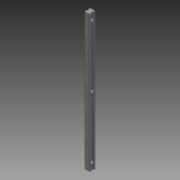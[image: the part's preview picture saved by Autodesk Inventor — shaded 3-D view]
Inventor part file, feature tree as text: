
AUTODESK INVENTOR PART (.ipt)
format: ipt  version: 2014 SP2 (Build 180246200, 246)  size: 133,120 bytes
history: native  units: mm
features: other x42, sketch x2, extrude x1, revolve x1, pattern_linear x1
ambient origin geometry x8: Origin, YZ Plane, XZ Plane, XY Plane, X Axis, Y Axis, Z Axis, Center Point
bodies: Solid1 (feature_tree)
feature tree (47):
  extrude  "Extrusion1"  TaperAngle=360.0deg  [1 undecoded]
  revolve  "Revolution1"  [1 undecoded]
  pattern_linear  "Rectangular Pattern1"  [2 undecoded]
  other  "to_ball_1_XY"
  other  "to_ball_1_YZ"
  other  "to_ball_1_ZX"
  other  "to_ball_1_X"
  other  "to_ball_1_Y"
  other  "to_ball_1_Z"
  other  "to_ball_1_Center"
  other  "to_ball_2_XY"
  other  "to_ball_2_YZ"
  other  "to_ball_2_ZX"
  other  "to_ball_2_X"
  other  "to_ball_2_Y"
  other  "to_ball_2_Z"
  other  "to_ball_2_Center"
  other  "to_ball_3_XY"
  other  "to_ball_3_YZ"
  other  "to_ball_3_ZX"
  other  "to_ball_3_X"
  other  "to_ball_3_Y"
  other  "to_ball_3_Z"
  other  "to_ball_3_Center"
  other  "to_ball_4_XY"
  other  "to_ball_4_YZ"
  other  "to_ball_4_ZX"
  other  "to_ball_4_X"
  other  "to_ball_4_Y"
  other  "to_ball_4_Z"
  other  "to_ball_4_Center"
  other  "to_body_XY"
  other  "to_body_YZ"
  other  "to_body_ZX"
  other  "to_body_X"
  other  "to_body_Y"
  other  "to_body_Z"
  other  "to_body_Center"
  other  "to_body2_XY"
  other  "to_body2_YZ"
  other  "to_body2_ZX"
  other  "to_body2_X"
  other  "to_body2_Y"
  other  "to_body2_Z"
  other  "to_body2_Center"
  sketch  "Sketch_1"  dims[d0=300.0mm d1=0.0mm d2=360.0deg]
  sketch  "Sketch_3"  dims[d3=30.0mm d5=135.0mm d6=10.0mm d8=0.0mm]
note: 4 required parameter values undecoded (feature->parameter linkage not recoverable at this tier; creation-order binding heuristic only, values carry confidence <= 0.55)
